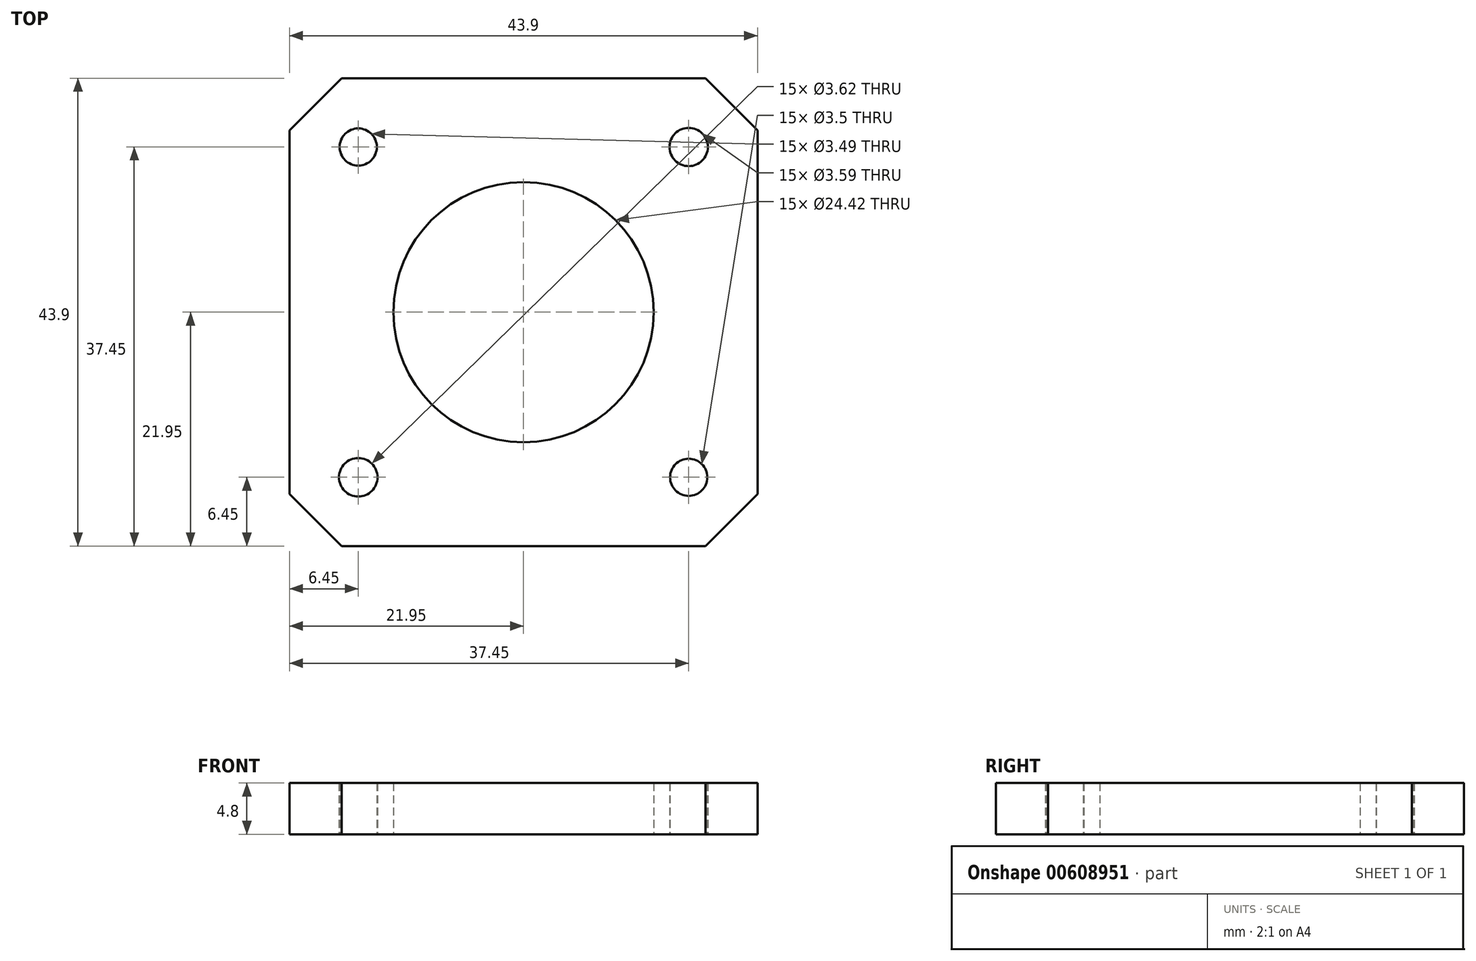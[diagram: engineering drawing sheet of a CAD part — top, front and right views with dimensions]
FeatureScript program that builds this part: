
annotation { "Feature Type Name" : "Feature", "Feature Type Description" : "" }
export const myFeature = defineFeature(function(context is Context, id is Id, definition is map)
    precondition{}
    {
        {
            var Q0;
            Q0=qCreatedBy(makeId("Top.planeOp"),FACE);
            var sketch = newSketch(context, id + "F0", { "sketchPlane" : qUnion([Q0])});
            skLineSegment(sketch, "E0.0", {"start": v(21.95, 17.07) * mm, "end": v(17.07, 21.95) * mm});
            skLineSegment(sketch, "E0.1", {"start": v(21.95, -17.07) * mm, "end": v(21.95, 17.07) * mm});
            skLineSegment(sketch, "E0.2", {"start": v(17.07, 21.95) * mm, "end": v(-17.07, 21.95) * mm});
            skLineSegment(sketch, "E0.3", {"start": v(17.07, -21.95) * mm, "end": v(21.95, -17.07) * mm});
            skLineSegment(sketch, "E0.4", {"start": v(-17.07, 21.95) * mm, "end": v(-21.95, 17.07) * mm});
            skLineSegment(sketch, "E0.5", {"start": v(-21.95, 17.07) * mm, "end": v(-21.95, -17.07) * mm});
            skLineSegment(sketch, "E0.6", {"start": v(-21.95, -17.07) * mm, "end": v(-17.07, -21.95) * mm});
            skLineSegment(sketch, "E0.7", {"start": v(-17.07, -21.95) * mm, "end": v(17.07, -21.95) * mm});
            skCircle(sketch, "E1", {"center": v(-15.5, -15.5) * mm, "radius": 1.8 * mm});
            skCircle(sketch, "E2", {"center": v(15.5, -15.5) * mm, "radius": 1.75 * mm});
            skCircle(sketch, "E3", {"center": v(-15.5, 15.5) * mm, "radius": 1.74 * mm});
            skCircle(sketch, "E4", {"center": v(15.5, 15.5) * mm, "radius": 1.8 * mm});
            skCircle(sketch, "E5", {"center": v(0, 0) * mm, "radius": 12.2 * mm});
            skSolve(sketch);
        }
        {
            var Q0;
            Q0=makeQuery(id+"F0.imprint","IMPRINT",FACE,{"disambiguationData":[TD([[makeQuery(id+"F0.imprint","IMPRINT",EDGE,{"derivedFrom":sQuery(id+"F0.wireOp",EDGE,"E0.0")}),1.0]])]});
            var Q1;
            Q1=sQuery(id+"F0.wireOp",EDGE,"E0.0");
            var Q2;
            Q2=sQuery(id+"F0.wireOp",EDGE,"E0.1");
            var Q3;
            Q3=sQuery(id+"F0.wireOp",EDGE,"E0.2");
            var Q4;
            Q4=sQuery(id+"F0.wireOp",EDGE,"E0.3");
            var Q5;
            Q5=sQuery(id+"F0.wireOp",EDGE,"E0.4");
            var Q6;
            Q6=sQuery(id+"F0.wireOp",EDGE,"E0.5");
            var Q7;
            Q7=sQuery(id+"F0.wireOp",EDGE,"E0.6");
            var Q8;
            Q8=sQuery(id+"F0.wireOp",EDGE,"E0.7");
            var Q9;
            Q9=sQuery(id+"F0.wireOp",EDGE,"E1");
            var Q10;
            Q10=sQuery(id+"F0.wireOp",EDGE,"E2");
            var Q11;
            Q11=sQuery(id+"F0.wireOp",EDGE,"E3");
            var Q12;
            Q12=sQuery(id+"F0.wireOp",EDGE,"E4");
            var Q13;
            Q13=sQuery(id+"F0.wireOp",EDGE,"E5");
            extrude(context, id + "F1", {"entities" : qUnion([Q0]), "surfaceEntities" : qUnion([Q1, Q2, Q3, Q4, Q5, Q6, Q7, Q8, Q9, Q10, Q11, Q12, Q13]), "depth" : 4.8 * mm, "offsetDistance" : 25 * mm});
        }
    });
